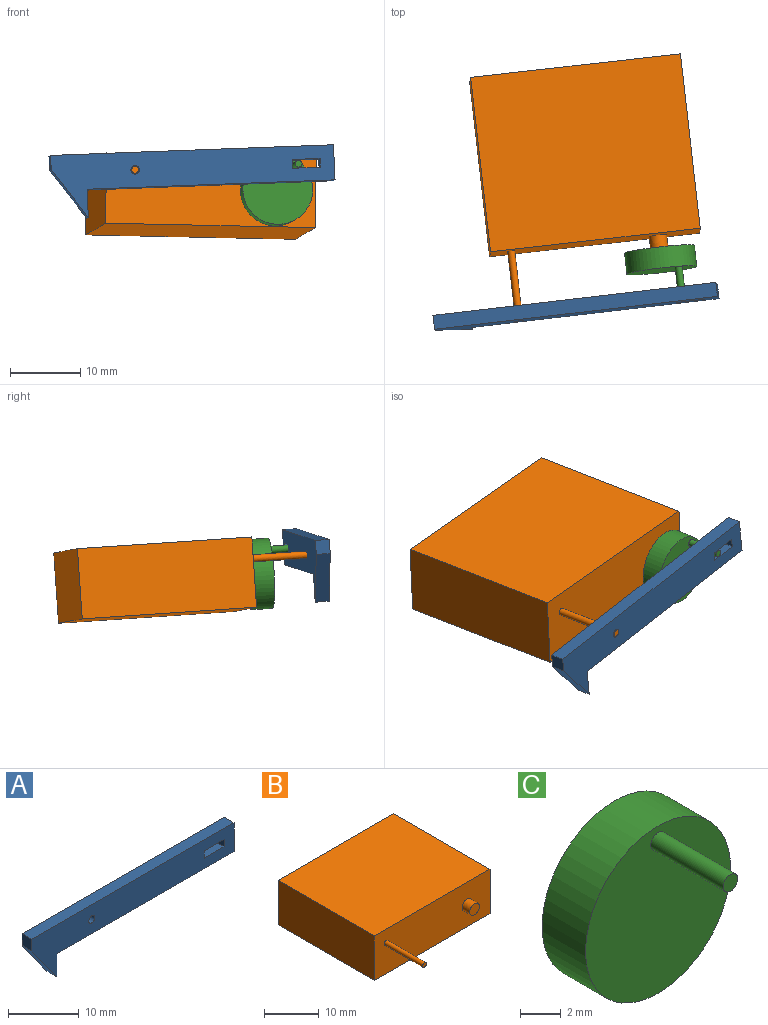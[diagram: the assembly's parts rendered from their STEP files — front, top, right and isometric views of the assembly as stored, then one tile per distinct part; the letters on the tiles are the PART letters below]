
ASSEMBLY  parts=3 mates=2
PART A: 13 faces, bbox 40.5x2x9 mm
  f0: plane 35.5x2mm, normal (0,0,-1), area 71mm2, adj f1,f4,f5,f6
  f1: plane 5x2mm, normal (1,0,0), area 10mm2, adj f0,f2,f4,f5
  f2: plane 40.5x2mm, normal (0,0,1), area 81mm2, adj f1,f3,f4,f5
  f3: plane 2x2mm, normal (-1,0,0), area 4mm2, adj f2,f4,f5,f7
  f4: plane 40.5x9mm, normal (0,-1,0), area 198.9mm2, adj f0,f1,f2,f3,f6,f7,f8,f9
  f5: plane 40.5x9mm, normal (0,1,0), area 198.9mm2, adj f0,f1,f2,f3,f6,f7,f8,f9
  f6: plane 4x2mm, normal (1,0,0), area 8mm2, adj f0,f4,f5,f7
  f7: plane 7x5mm, normal (-0.81,0,-0.58), area 17.2mm2, adj f3,f4,f5,f6
  f8: plane 2x1.25mm, normal (-1,0,0), area 2.5mm2, adj f4,f5,f9,f11
  f9: plane 4x2mm, normal (0,0,-1), area 8mm2, adj f4,f5,f8,f10
  f10: plane 2x1.25mm, normal (1,0,0), area 2.5mm2, adj f4,f5,f9,f11
  f11: plane 4x2mm, normal (0,0,1), area 8mm2, adj f4,f5,f8,f10
  f12: cylinder r=0.6mm len=2mm, axis (0,-1,0), area 7.5mm2, adj f4,f5
PART B: 10 faces, bbox 30x35x10 mm
  f0: plane 25x10mm, normal (-1,0,0), area 250mm2, adj f1,f3,f4,f5
  f1: plane 30x25mm, normal (0,0,-1), area 750mm2, adj f0,f2,f4,f5
  f2: plane 25x10mm, normal (1,0,0), area 250mm2, adj f1,f3,f4,f5
  f3: plane 30x25mm, normal (0,0,1), area 750mm2, adj f0,f2,f4,f5
  f4: plane 30x10mm, normal (0,1,0), area 300mm2, adj f0,f1,f2,f3
  f5: plane 30x10mm, normal (0,-1,0), area 294.3mm2, adj f0,f1,f2,f3,f6,f8
  f6: cylinder r=1.25mm len=2.5mm, axis (0,1,0), area 15.7mm2, adj f5,f7
  f7: plane 2.5x2.5mm, normal (0,-1,0), area 4.9mm2, adj f6
  f8: cylinder r=0.5mm len=10mm, axis (0,1,0), area 31.4mm2, adj f5,f9
  f9: plane 1x1mm, normal (0,-1,0), area 0.8mm2, adj f8
PART C: 5 faces, bbox 10x8x10 mm
  f0: cylinder r=5mm len=10mm, axis (0,1,0), area 94.2mm2, adj f1,f2
  f1: plane 10x10mm, normal (0,-1,0), area 77.8mm2, adj f0,f3
  f2: plane 10x10mm, normal (0,1,0), area 78.5mm2, adj f0
  f3: cylinder r=0.5mm len=5mm, axis (0,1,0), area 15.7mm2, adj f1,f4
  f4: plane 1x1mm, normal (0,-1,0), area 0.8mm2, adj f3
PLACE A rot(axis=(-0.47,-0.3,0.83),7.9deg) t=(-23.09,-20.17,7.04)mm
PLACE B rot(axis=(-0.51,0.13,0.85),7.6deg) t=(-9.77,-11.05,0.06)mm
PLACE C rot(axis=(-0.16,0.98,0.14),36.7deg) t=(-31.33,-15.15,5.64)mm
MATE revolute C.f0 <-> B.f6  axis (-0.11,0.99,-0.07) through (-31.33,-15.15,5.64)mm
MATE revolute A.f12 <-> B.f8  axis (0.11,-0.99,0.07) through (-51.27,-25.3,8.6)mm
